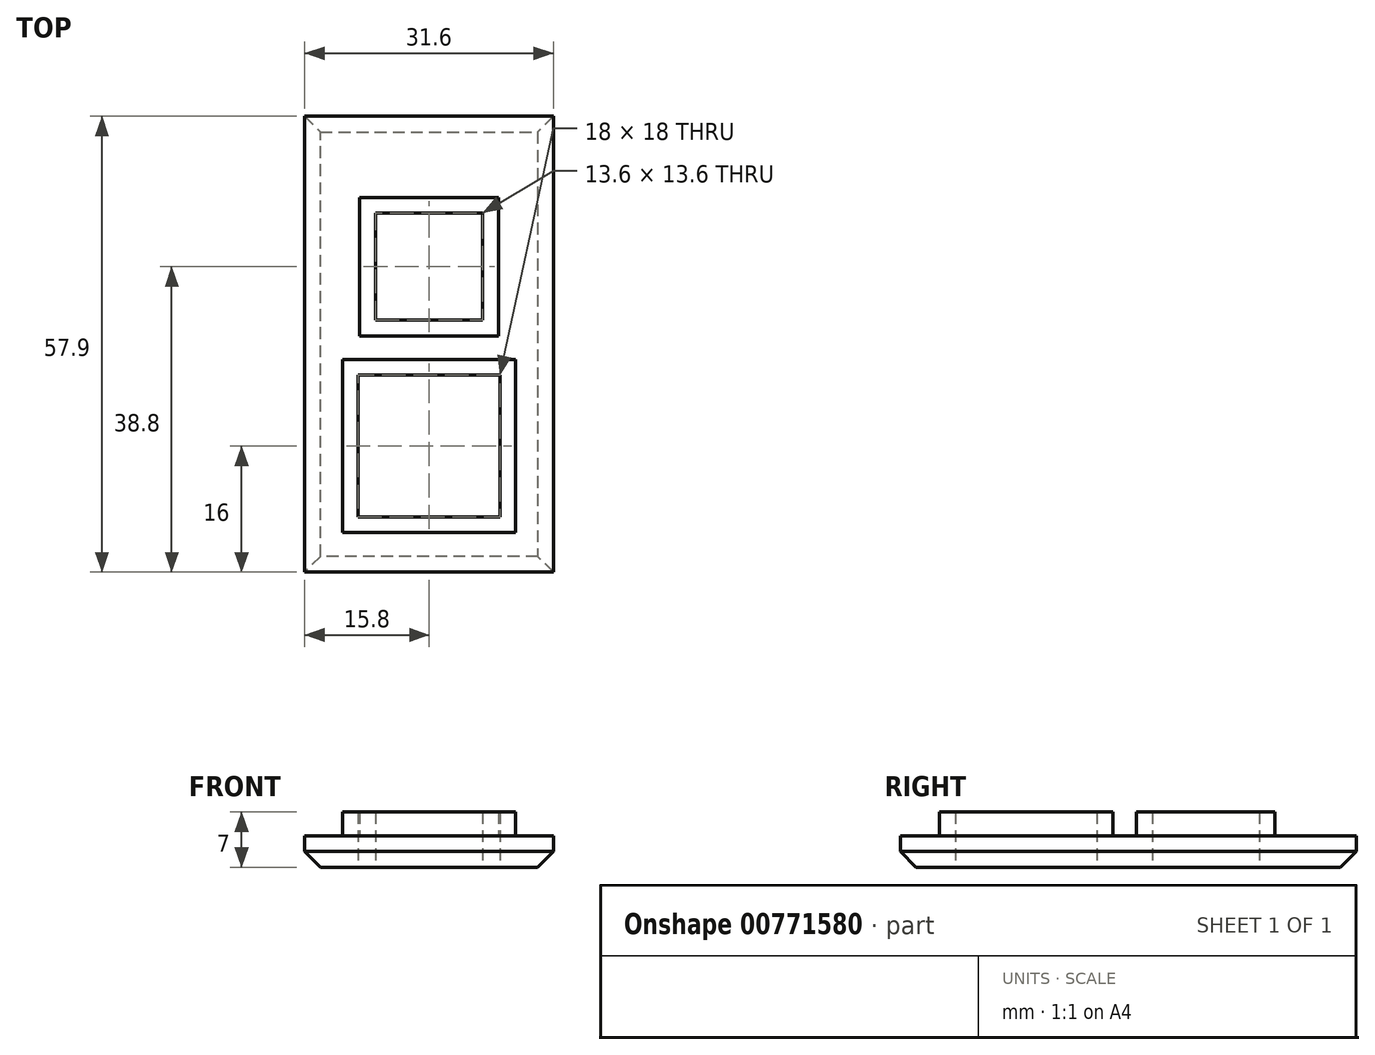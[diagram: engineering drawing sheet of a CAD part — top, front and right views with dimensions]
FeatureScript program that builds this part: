
annotation { "Feature Type Name" : "Feature", "Feature Type Description" : "" }
export const myFeature = defineFeature(function(context is Context, id is Id, definition is map)
    precondition{}
    {
        {
            var Q0;
            Q0=qCreatedBy(makeId("Top.planeOp"),FACE);
            var sketch = newSketch(context, id + "F0", { "sketchPlane" : qUnion([Q0])});
            skLineSegment(sketch, "E0.bottom", {"start": v(0, 0) * mm, "end": v(-25.6, 0) * mm});
            skLineSegment(sketch, "E0.top", {"start": v(0, 51.9) * mm, "end": v(-25.6, 51.9) * mm});
            skLineSegment(sketch, "E0.left", {"start": v(0, 0) * mm, "end": v(0, 51.9) * mm});
            skLineSegment(sketch, "E0.right", {"start": v(-25.6, 0) * mm, "end": v(-25.6, 51.9) * mm});
            skLineSegment(sketch, "E1.bottom", {"start": v(-21.8, 4) * mm, "end": v(-3.8, 4) * mm});
            skLineSegment(sketch, "E1.top", {"start": v(-21.8, 22) * mm, "end": v(-3.8, 22) * mm});
            skLineSegment(sketch, "E1.left", {"start": v(-21.8, 4) * mm, "end": v(-21.8, 22) * mm});
            skLineSegment(sketch, "E1.right", {"start": v(-3.8, 4) * mm, "end": v(-3.8, 22) * mm});
            skLineSegment(sketch, "E2.bottom", {"start": v(-19.6, 29) * mm, "end": v(-6, 29) * mm});
            skLineSegment(sketch, "E2.top", {"start": v(-19.6, 42.6) * mm, "end": v(-6, 42.6) * mm});
            skLineSegment(sketch, "E2.left", {"start": v(-19.6, 29) * mm, "end": v(-19.6, 42.6) * mm});
            skLineSegment(sketch, "E2.right", {"start": v(-6, 29) * mm, "end": v(-6, 42.6) * mm});
            skLineSegment(sketch, "E3.0", {"start": v(-28.6, -3) * mm, "end": v(-28.6, 54.9) * mm});
            skLineSegment(sketch, "E3.1", {"start": v(3, -3) * mm, "end": v(-28.6, -3) * mm});
            skLineSegment(sketch, "E3.2", {"start": v(3, -3) * mm, "end": v(3, 54.9) * mm});
            skLineSegment(sketch, "E3.3", {"start": v(3, 54.9) * mm, "end": v(-28.6, 54.9) * mm});
            skLineSegment(sketch, "E4.0", {"start": v(-21.6, 27) * mm, "end": v(-21.6, 44.6) * mm});
            skLineSegment(sketch, "E4.1", {"start": v(-21.6, 27) * mm, "end": v(-4, 27) * mm});
            skLineSegment(sketch, "E4.2", {"start": v(-4, 27) * mm, "end": v(-4, 44.6) * mm});
            skLineSegment(sketch, "E4.3", {"start": v(-21.6, 44.6) * mm, "end": v(-4, 44.6) * mm});
            skLineSegment(sketch, "E5.0", {"start": v(-23.8, 24) * mm, "end": v(-1.8, 24) * mm});
            skLineSegment(sketch, "E5.1", {"start": v(-23.8, 2) * mm, "end": v(-23.8, 24) * mm});
            skLineSegment(sketch, "E5.2", {"start": v(-23.8, 2) * mm, "end": v(-1.8, 2) * mm});
            skLineSegment(sketch, "E5.3", {"start": v(-1.8, 2) * mm, "end": v(-1.8, 24) * mm});
            skLineSegment(sketch, "E6", {"start": v(-25.6, 13) * mm, "end": v(-21.8, 13) * mm, "construction": true});
            skLineSegment(sketch, "E7", {"start": v(-3.8, 13) * mm, "end": v(0, 13) * mm, "construction": true});
            skSolve(sketch);
        }
        {
            assignVariable(context, id + "F1", {"name" : "t", "anyValue" : 4});
        }
        {
            var Q0;
            Q0=makeQuery(id+"F0.imprint","IMPRINT",FACE,{"disambiguationData":[TD([[makeQuery(id+"F0.imprint","IMPRINT",EDGE,{"derivedFrom":sQuery(id+"F0.wireOp",EDGE,"E0.bottom")}),-1.0]])]});
            var Q1;
            Q1=makeQuery(id+"F0.imprint","IMPRINT",FACE,{"disambiguationData":[TD([[makeQuery(id+"F0.imprint","IMPRINT",EDGE,{"derivedFrom":sQuery(id+"F0.wireOp",EDGE,"E1.bottom")}),-1.0]])]});
            var Q2;
            Q2=makeQuery(id+"F0.imprint","IMPRINT",FACE,{"disambiguationData":[TD([[makeQuery(id+"F0.imprint","IMPRINT",EDGE,{"derivedFrom":sQuery(id+"F0.wireOp",EDGE,"E2.bottom")}),-1.0]])]});
            var Q3;
            Q3=makeQuery(id+"F0.imprint","IMPRINT",FACE,{"disambiguationData":[TD([[makeQuery(id+"F0.imprint","IMPRINT",EDGE,{"derivedFrom":sQuery(id+"F0.wireOp",EDGE,"E0.bottom")}),1.0]])]});
            extrude(context, id + "F2", {"entities" : qUnion([Q0, Q1, Q2, Q3]), "depth" : (getVariable(context, 't')) * mm, "offsetDistance" : 25 * mm});
        }
        {
            var Q0;
            Q0=makeQuery(id+"F0.imprint","IMPRINT",FACE,{"disambiguationData":[TD([[makeQuery(id+"F0.imprint","IMPRINT",EDGE,{"derivedFrom":sQuery(id+"F0.wireOp",EDGE,"E2.bottom")}),-1.0]])]});
            var Q1;
            Q1=makeQuery(id+"F0.imprint","IMPRINT",FACE,{"disambiguationData":[TD([[makeQuery(id+"F0.imprint","IMPRINT",EDGE,{"derivedFrom":sQuery(id+"F0.wireOp",EDGE,"E1.bottom")}),-1.0]])]});
            extrude(context, id + "F3", {"entities" : qUnion([Q0, Q1]), "operationType" : NewBodyOperationType.ADD, "depth" : (getVariable(context, 't') + 3) * mm, "offsetDistance" : 25 * mm, "hasSecondDirection" : true, "secondDirectionOppositeDirection" : false, "secondDirectionDepth" : (getVariable(context, 't')) * mm});
        }
        {
            var Q0;
            Q0=makeQuery(id+"F2.opExtrude","CAP_EDGE",EDGE,{"disambiguationData":[OSD([sQuery(id+"F0.wireOp",EDGE,"E3.0")])],"isStart":true});
            var Q1;
            Q1=makeQuery(id+"F2.opExtrude","CAP_EDGE",EDGE,{"disambiguationData":[OSD([sQuery(id+"F0.wireOp",EDGE,"E3.1")])],"isStart":true});
            var Q2;
            Q2=makeQuery(id+"F2.opExtrude","CAP_EDGE",EDGE,{"disambiguationData":[OSD([sQuery(id+"F0.wireOp",EDGE,"E3.2")])],"isStart":true});
            var Q3;
            Q3=makeQuery(id+"F2.opExtrude","CAP_EDGE",EDGE,{"disambiguationData":[OSD([sQuery(id+"F0.wireOp",EDGE,"E3.3")])],"isStart":true});
            chamfer(context, id + "F4", {"entities" : qUnion([Q0, Q1, Q2, Q3]), "width" : 2 * mm, "tangentPropagation" : true});
        }
    });
